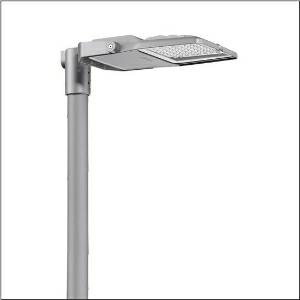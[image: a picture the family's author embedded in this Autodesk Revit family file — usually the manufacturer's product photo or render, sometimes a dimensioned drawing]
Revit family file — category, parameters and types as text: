
# Revit family: floodlight_fl_21_iq_mini___pl64_5xa7772c4e3a_b66a
name_source: partatom
category: Lighting Fixtures
units: mm (PartAtom-declared; Revit-internal decimal feet)

## family parameters
Cut with Voids When Loaded = No
Host = Face
Light Source = No
Part Type = Normal
Room Calculation Point = No
Round Connector Dimension = Use Diameter
Shared = No

## types (1)
- --- (1 x LED, 12280 lm, 87.2 W, 4000K)
    Apparent Load = 87 VA
    CIE Flux Codes = 28 80 98 100 100
    Color Rendering = 70
    Color Temperature = 4000K
    Default Elevation = 1800 mm
    Description = Floodlight FL 21 iQ mini, floodlight, primary light control with lens, of PMMA, primary optical cover: protective disc, of toughened safety glass, transparent, light distribution: PL64, light emission: direct distribution, installation type: surface-mounted, lamps: LED, High Power LED, rated values: 12.280lm | 87,2W | 140,8lm/W (begin service life); end service life: 12.280lm | 92,1W; at 50% lumin. flux: 6.140lm | 40,2W | 152,7lm/W, colour temperature: 4000K, colour rendering: CRI > 70, light colour: 740, light setting 1 begin service life: 100% | 12.280lm | 87,2W | 140,8lm/W | 4.000K, light setting 1 end service life: 92,1W, further light settings possible, control: pre-setting: linear dimming characteristic, Auto-Match, Temp-Guard, Night-Set, Smart-Wire, Desk-Remote (wireless, voltage-free reading and setting of iQ features in the workshop via application-optimized NFC function/RFID function), optimised constant luminous flux control (CLO 2.0), Light-Fading, Lumen-Switch, with terminal, 6-pole, mains connection: 220..240V, AC, 50/60Hz, luminaire housing, of diecast aluminium, powder-coated, SITECO metallic grey (DB 702S), corrosivity category C5 mid according to DIN EN ISO 12944suitable for swimming poolschlorine-resistant, sealing non-destructively replaceable, please order mast flange separately, mast bracket, of steel, galvanised, powder-coated, protection rating (complete): IP66, insulation class (complete): insulation class II (safety insulation), certification: CE, ENEC, VDE, protection symbol: D, impact resistance: IK08, permissible operating ambient temperature: -40..+40°C, permissible operating ambient temperature for outdoor applications: -40..+50°C, standard: DIN EN 12944, LABS conformity tested according to VDMA 24364:2018-05, packaging unit: 1 piece

Light Distribution: PL64
    Height = 70 mm
    Lamp = 1 x LED
    Lamp Light Flux = 12280 lm
    Lamp Power = 87.2 W
    Lamp count = 1
    Length = 485 mm
    Luminous efficacy = 141 lm/W
    Manufacturer = Siteco
    ModVariant = No
    Model = 5XA7772C4E3A
    Number of Poles = 1
    OnlyDefault = Yes
    Power Factor = 1
    Product Name = Floodlight FL 21 iQ mini | PL64
    Product group = floodlight | pylon annexe
    ProductGroupID = 6201
    Protection Class = Protection class II
    Protection Degree = IP 66
    RLX_Detail_Level = 1
    RLX_Emergency_Light_Flux = 0 lm
    RLX_Emergency_Type = 0
    RLX_Emergency_Type_DB = No
    RlxData = <blob elided: 101633 chars, md5=9a5c4eaa>
    Socket = socket
    Standby Power = 0 W
    System Light Flux = 12280 lm
    System Power = 87 W
    Type Comments = factory setting: luminous flux: 100 % | dim-lin: 254 | 456 mA
    Type Image = l_1007125.jpg
    URL = http://relux.com
    VarID = @adj_165695
    Voltage = 0 V
    Weight = 0.00 kg
    Width = 337 mm

## geometry (parser evidence)
native form markers: Blend x4, Sweep x13
no freeform markers — native parametric forms only
